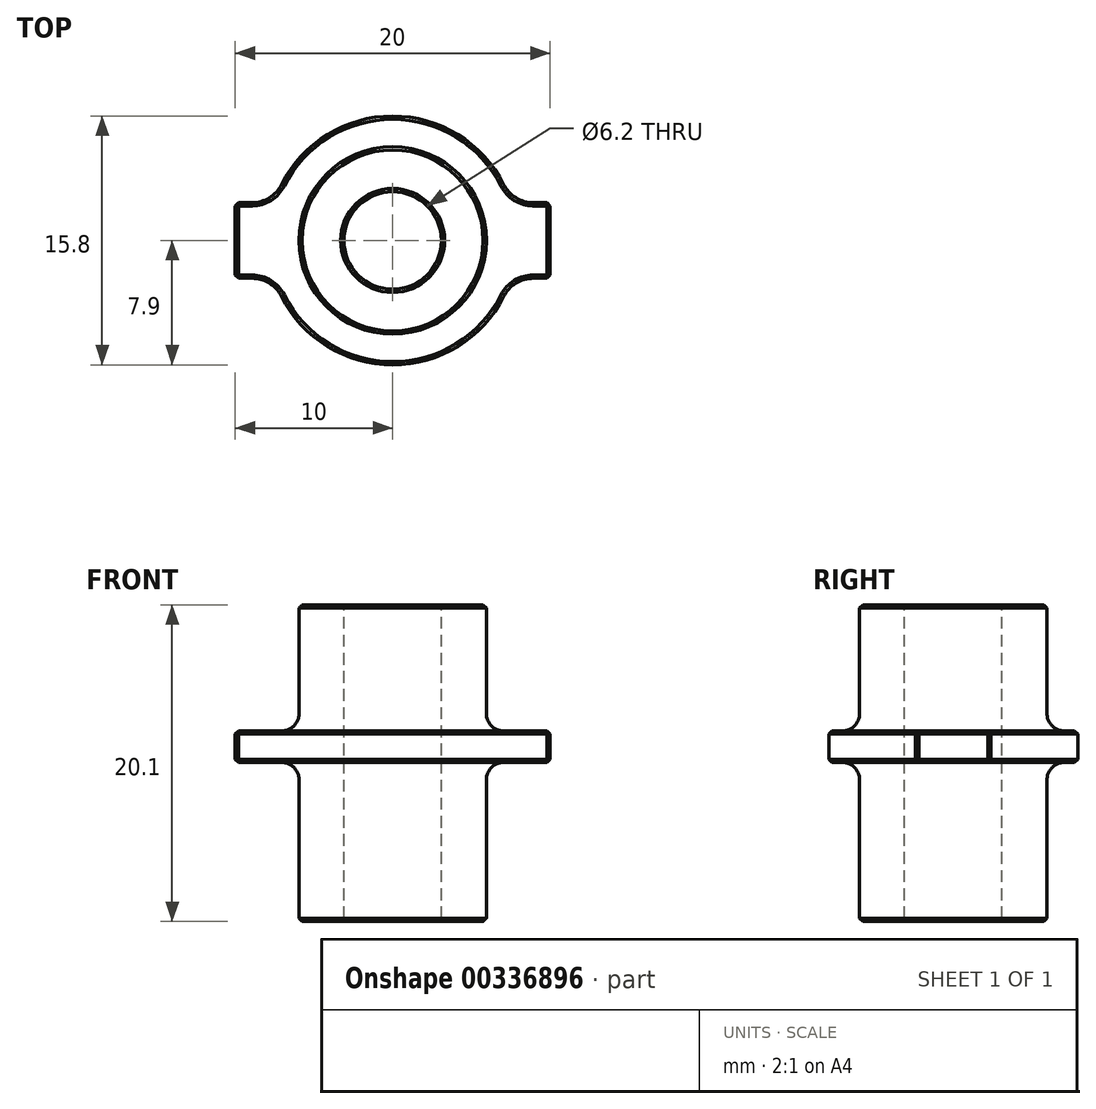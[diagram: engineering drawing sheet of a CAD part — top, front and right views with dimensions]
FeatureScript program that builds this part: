
annotation { "Feature Type Name" : "Feature", "Feature Type Description" : "" }
export const myFeature = defineFeature(function(context is Context, id is Id, definition is map)
    precondition{}
    {
        {
            var Q0;
            Q0=qCreatedBy(makeId("Front.planeOp"),FACE);
            var sketch = newSketch(context, id + "F0", { "sketchPlane" : qUnion([Q0])});
            skLineSegment(sketch, "E0", {"start": v(0, 0) * mm, "end": v(0, -12.1) * mm, "construction": true});
            skLineSegment(sketch, "E1", {"start": v(3.1, -12.1) * mm, "end": v(5.95, -12.1) * mm});
            skLineSegment(sketch, "E2", {"start": v(5.95, -2) * mm, "end": v(7.9, -2) * mm});
            skLineSegment(sketch, "E3", {"start": v(7.9, -2) * mm, "end": v(7.9, 0) * mm});
            skLineSegment(sketch, "E4", {"start": v(7.9, 0) * mm, "end": v(5.95, 0) * mm});
            skLineSegment(sketch, "E5", {"start": v(3.1, -12.1) * mm, "end": v(3.1, 0) * mm});
            skLineSegment(sketch, "E6.MirrorCS", {"start": v(-7.9, -2) * mm, "end": v(-7.9, 0) * mm, "construction": true});
            skLineSegment(sketch, "E7.MirrorCS", {"start": v(-3.1, -12.1) * mm, "end": v(-3.1, 0) * mm, "construction": true});
            skLineSegment(sketch, "E8", {"start": v(5.95, -12.1) * mm, "end": v(5.95, -2) * mm});
            skLineSegment(sketch, "E9.MirrorCS", {"start": v(-5.95, -12.1) * mm, "end": v(-5.95, -2) * mm});
            skLineSegment(sketch, "E10", {"start": v(5.95, -2) * mm, "end": v(5.95, 0) * mm, "construction": true});
            skLineSegment(sketch, "E11", {"start": v(5.95, 0) * mm, "end": v(5.95, 8) * mm});
            skLineSegment(sketch, "E12", {"start": v(5.95, 8) * mm, "end": v(3.1, 8) * mm});
            skLineSegment(sketch, "E13", {"start": v(3.1, 0) * mm, "end": v(3.1, 8) * mm});
            skSolve(sketch);
        }
        {
            var Q0;
            Q0=makeQuery(id+"F0.imprint","IMPRINT",FACE,{"disambiguationData":[TD([[makeQuery(id+"F0.imprint","IMPRINT",EDGE,{"derivedFrom":sQuery(id+"F0.wireOp",EDGE,"E1")}),1.0]])]});
            var Q1;
            Q1=sQuery(id+"F0.wireOp",EDGE,"E0");
            revolve(context, id + "F1", {"entities" : qUnion([Q0]), "axis" : qUnion([Q1]), "revolveType" : RevolveType.FULL});
        }
        {
            var Q0;
            Q0=makeQuery(id+"F1.opRevolve","SWEPT_FACE",FACE,{"disambiguationData":[OSD([sQuery(id+"F0.wireOp",EDGE,"E4")])]});
            var sketch = newSketch(context, id + "F2", { "sketchPlane" : qUnion([Q0])});
            skLineSegment(sketch, "E14.bottom", {"start": v(3.1, 2.4) * mm, "end": v(10, 2.4) * mm});
            skLineSegment(sketch, "E14.top", {"start": v(3.1, -2.4) * mm, "end": v(10, -2.4) * mm});
            skLineSegment(sketch, "E14.left", {"start": v(0, 2.4) * mm, "end": v(0, -2.4) * mm, "construction": true});
            skLineSegment(sketch, "E14.right", {"start": v(10, 2.4) * mm, "end": v(10, -2.4) * mm});
            skLineSegment(sketch, "E15", {"start": v(3.1, 2.4) * mm, "end": v(3.1, -2.4) * mm});
            skLineSegment(sketch, "E16.MirrorCS", {"start": v(-10, 2.4) * mm, "end": v(-10, -2.4) * mm});
            skLineSegment(sketch, "E17.MirrorCS", {"start": v(-3.1, 2.4) * mm, "end": v(-10, 2.4) * mm});
            skLineSegment(sketch, "E18.MirrorCS", {"start": v(-3.1, -2.4) * mm, "end": v(-10, -2.4) * mm});
            skLineSegment(sketch, "E19.MirrorCS", {"start": v(-3.1, 2.4) * mm, "end": v(-3.1, -2.4) * mm});
            skSolve(sketch);
        }
        {
            var Q0;
            Q0 = qSketchRegion(id + "F2", true);
            extrude(context, id + "F3", {"entities" : qUnion([Q0]), "operationType" : NewBodyOperationType.ADD, "oppositeDirection" : true, "depth" : 2 * mm});
        }
        {
            var Q0;
            Q0=makeQuery(id+"F3.boolean.opBoolean","INTERSECT",EDGE,{"derivedFrom":[makeQuery(id+"F1.opRevolve","SWEPT_FACE",FACE,{"disambiguationData":[OSD([sQuery(id+"F0.wireOp",EDGE,"E3")])]}),makeQuery(id+"F3.opExtrude","SWEPT_FACE",FACE,{"disambiguationData":[OSD([sQuery(id+"F2.wireOp",EDGE,"E14.top")])]})]});
            var Q1;
            Q1=makeQuery(id+"F3.boolean.opBoolean","INTERSECT",EDGE,{"derivedFrom":[makeQuery(id+"F1.opRevolve","SWEPT_FACE",FACE,{"disambiguationData":[OSD([sQuery(id+"F0.wireOp",EDGE,"E3")])]}),makeQuery(id+"F3.opExtrude","SWEPT_FACE",FACE,{"disambiguationData":[OSD([sQuery(id+"F2.wireOp",EDGE,"E14.bottom")])]})]});
            var Q2;
            Q2=makeQuery(id+"F3.boolean.opBoolean","INTERSECT",EDGE,{"derivedFrom":[makeQuery(id+"F1.opRevolve","SWEPT_FACE",FACE,{"disambiguationData":[OSD([sQuery(id+"F0.wireOp",EDGE,"E3")])]}),makeQuery(id+"F3.opExtrude","SWEPT_FACE",FACE,{"disambiguationData":[OSD([sQuery(id+"F2.wireOp",EDGE,"E17.MirrorCS")])]})]});
            var Q3;
            Q3=makeQuery(id+"F3.boolean.opBoolean","INTERSECT",EDGE,{"derivedFrom":[makeQuery(id+"F1.opRevolve","SWEPT_FACE",FACE,{"disambiguationData":[OSD([sQuery(id+"F0.wireOp",EDGE,"E3")])]}),makeQuery(id+"F3.opExtrude","SWEPT_FACE",FACE,{"disambiguationData":[OSD([sQuery(id+"F2.wireOp",EDGE,"E18.MirrorCS")])]})]});
            fillet(context, id + "F4", {"entities" : qUnion([Q0, Q1, Q2, Q3]), "radius" : 2.1 * mm, "tangentPropagation" : true, "allowEdgeOverflow" : false});
        }
        {
            var Q0;
            Q0=makeQuery(id+"F1.opRevolve","SWEPT_FACE",FACE,{"disambiguationData":[OSD([sQuery(id+"F0.wireOp",EDGE,"E5")])]});
            var Q1;
            Q1=makeQuery(id+"F1.opRevolve","SWEPT_FACE",FACE,{"disambiguationData":[OSD([sQuery(id+"F0.wireOp",EDGE,"e067fc40-9af5-4b76-accb-063485be59212.MirrorCS")])]});
            var Q2;
            Q2=makeQuery(id+"F3.opExtrude","SWEPT_FACE",FACE,{"disambiguationData":[OSD([sQuery(id+"F2.wireOp",EDGE,"E14.right")])]});
            var Q3;
            Q3=makeQuery(id+"F1.opRevolve","SWEPT_EDGE",EDGE,{"disambiguationData":[OSD([sQuery(id+"F0.wireOp",EDGE,"E2"),sQuery(id+"F0.wireOp",EDGE,"E3")])]});
            var Q4;
            Q4=makeQuery(id+"F1.opRevolve","SWEPT_EDGE",EDGE,{"disambiguationData":[OSD([sQuery(id+"F0.wireOp",EDGE,"E4"),sQuery(id+"F0.wireOp",EDGE,"E3")])]});
            var Q5;
            Q5=makeQuery(id+"F3.opExtrude","CAP_EDGE",EDGE,{"disambiguationData":[OSD([sQuery(id+"F2.wireOp",EDGE,"E14.top")])],"isStart":true});
            var Q6;
            Q6=makeQuery(id+"F3.opExtrude","CAP_EDGE",EDGE,{"disambiguationData":[OSD([sQuery(id+"F2.wireOp",EDGE,"E14.top")])],"isStart":false});
            var Q7;
            Q7=makeQuery(id+"F3.opExtrude","CAP_EDGE",EDGE,{"disambiguationData":[OSD([sQuery(id+"F2.wireOp",EDGE,"E14.bottom")])],"isStart":true});
            var Q8;
            Q8=makeQuery(id+"F3.opExtrude","CAP_EDGE",EDGE,{"disambiguationData":[OSD([sQuery(id+"F2.wireOp",EDGE,"E14.bottom")])],"isStart":false});
            var Q9;
            Q9=makeQuery(id+"F3.opExtrude","SWEPT_FACE",FACE,{"disambiguationData":[OSD([sQuery(id+"F2.wireOp",EDGE,"E16.MirrorCS")])]});
            var Q10;
            Q10=makeQuery(id+"F3.opExtrude","CAP_EDGE",EDGE,{"disambiguationData":[OSD([sQuery(id+"F2.wireOp",EDGE,"E18.MirrorCS")])],"isStart":true});
            var Q11;
            Q11=makeQuery(id+"F3.opExtrude","CAP_EDGE",EDGE,{"disambiguationData":[OSD([sQuery(id+"F2.wireOp",EDGE,"E18.MirrorCS")])],"isStart":false});
            var Q12;
            Q12=makeQuery(id+"F3.opExtrude","CAP_EDGE",EDGE,{"disambiguationData":[OSD([sQuery(id+"F2.wireOp",EDGE,"E17.MirrorCS")])],"isStart":false});
            var Q13;
            Q13=makeQuery(id+"F3.opExtrude","CAP_EDGE",EDGE,{"disambiguationData":[OSD([sQuery(id+"F2.wireOp",EDGE,"E17.MirrorCS")])],"isStart":true});
            var Q14;
            Q14=makeQuery(id+"F1.opRevolve","SWEPT_EDGE",EDGE,{"disambiguationData":[OSD([sQuery(id+"F0.wireOp",EDGE,"E11"),sQuery(id+"F0.wireOp",EDGE,"E12")])]});
            var Q15;
            Q15=makeQuery(id+"F1.opRevolve","SWEPT_EDGE",EDGE,{"disambiguationData":[OSD([sQuery(id+"F0.wireOp",EDGE,"E1"),sQuery(id+"F0.wireOp",EDGE,"E8")])]});
            chamfer(context, id + "F5", {"entities" : qUnion([Q0, Q1, Q2, Q3, Q4, Q5, Q6, Q7, Q8, Q9, Q10, Q11, Q12, Q13, Q14, Q15]), "width" : 0.2 * mm, "tangentPropagation" : true});
        }
        {
            var Q0;
            Q0=makeQuery(id+"F3.boolean.opBoolean","INTERSECT",EDGE,{"derivedFrom":[makeQuery(id+"F3.opExtrude","CAP_FACE",FACE,{"disambiguationData":[OSD([sQuery(id+"F2.wireOp",EDGE,"E14.bottom"),sQuery(id+"F2.wireOp",EDGE,"E14.top"),sQuery(id+"F2.wireOp",EDGE,"E14.right"),sQuery(id+"F2.wireOp",EDGE,"E15")])],"isStart":false}),makeQuery(id+"F3.opExtrude","CAP_FACE",FACE,{"disambiguationData":[OSD([sQuery(id+"F2.wireOp",EDGE,"E16.MirrorCS"),sQuery(id+"F2.wireOp",EDGE,"E17.MirrorCS"),sQuery(id+"F2.wireOp",EDGE,"E18.MirrorCS"),sQuery(id+"F2.wireOp",EDGE,"E19.MirrorCS")])],"isStart":false})]});
            var Q1;
            Q1=makeQuery(id+"F3.boolean.opBoolean","INTERSECT",EDGE,{"derivedFrom":[makeQuery(id+"F3.opExtrude","CAP_FACE",FACE,{"disambiguationData":[OSD([sQuery(id+"F2.wireOp",EDGE,"E14.bottom"),sQuery(id+"F2.wireOp",EDGE,"E14.top"),sQuery(id+"F2.wireOp",EDGE,"E14.right"),sQuery(id+"F2.wireOp",EDGE,"E15")])],"isStart":true}),makeQuery(id+"F3.opExtrude","CAP_FACE",FACE,{"disambiguationData":[OSD([sQuery(id+"F2.wireOp",EDGE,"E16.MirrorCS"),sQuery(id+"F2.wireOp",EDGE,"E17.MirrorCS"),sQuery(id+"F2.wireOp",EDGE,"E18.MirrorCS"),sQuery(id+"F2.wireOp",EDGE,"E19.MirrorCS")])],"isStart":true})]});
            fillet(context, id + "F6", {"entities" : qUnion([Q0, Q1]), "radius" : 1.1 * mm, "tangentPropagation" : true, "defaultsChanged" : false, "vertexSettings" : [], "allowEdgeOverflow" : false});
        }
    });
